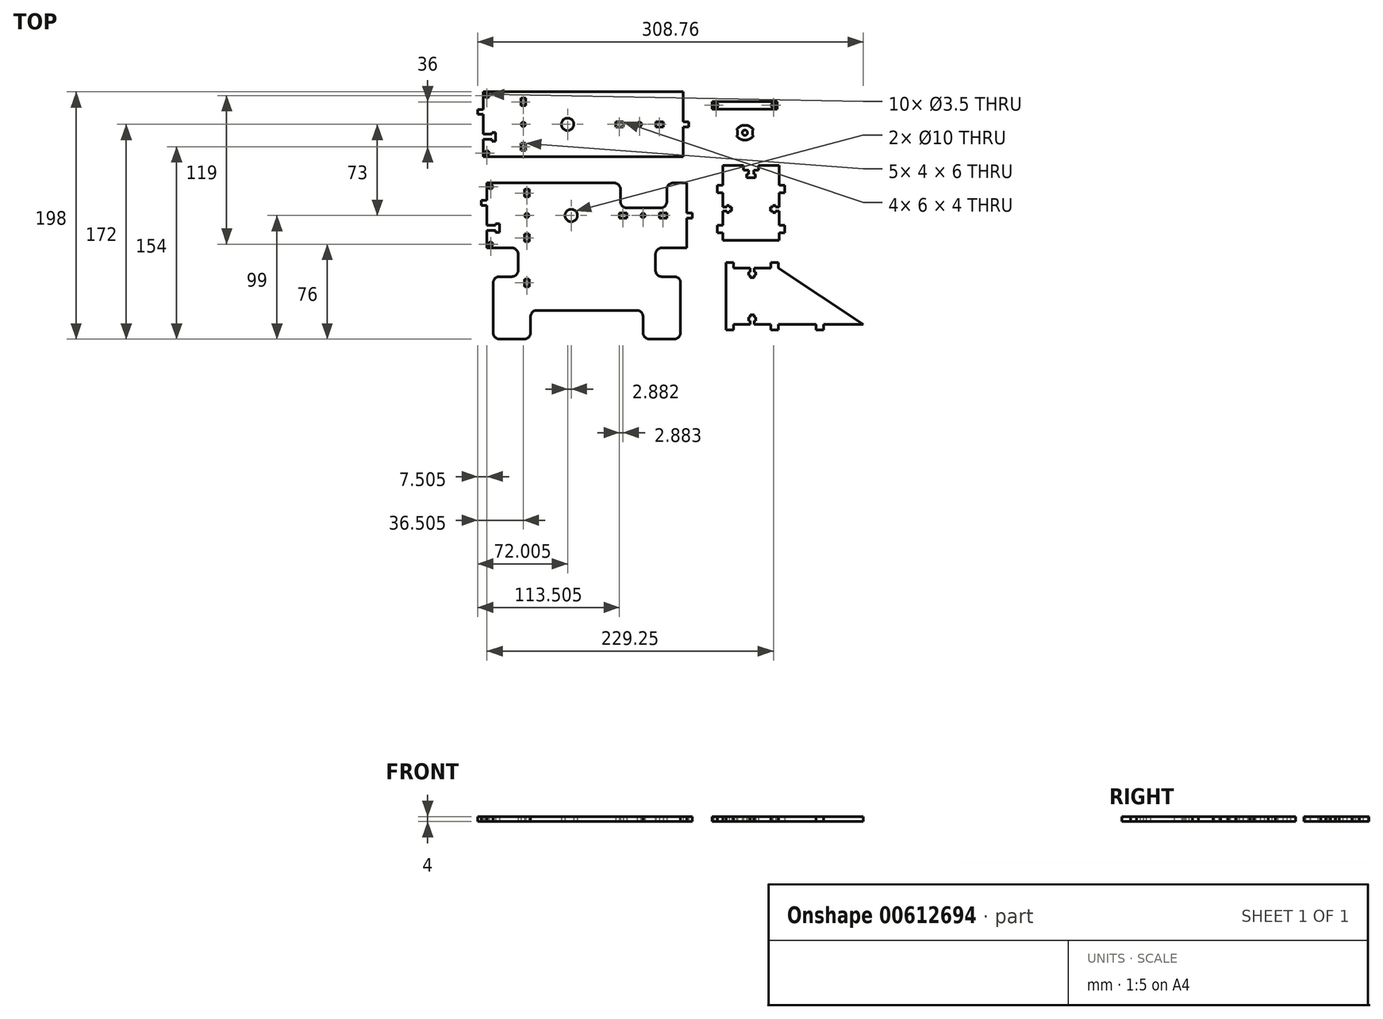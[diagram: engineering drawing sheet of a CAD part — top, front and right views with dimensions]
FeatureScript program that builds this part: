
annotation { "Feature Type Name" : "Feature", "Feature Type Description" : "" }
export const myFeature = defineFeature(function(context is Context, id is Id, definition is map)
    precondition{}
    {
        {
            var Q0;
            Q0=qCreatedBy(makeId("Top.planeOp"),FACE);
            var sketch = newSketch(context, id + "F0", { "sketchPlane" : qUnion([Q0])});
            skLineSegment(sketch, "E0", {"start": v(-149.88, 65.1) * mm, "end": v(-149.88, 81) * mm});
            skLineSegment(sketch, "E1", {"start": v(-149.88, 47) * mm, "end": v(-149.88, 60.9) * mm});
            skLineSegment(sketch, "E2", {"start": v(-149.88, 85) * mm, "end": v(-149.88, 99) * mm});
            skLineSegment(sketch, "E3", {"start": v(-147, -26) * mm, "end": v(-147, -12.1) * mm});
            skLineSegment(sketch, "E4", {"start": v(-147, -7.9) * mm, "end": v(-147, 8) * mm});
            skLineSegment(sketch, "E5", {"start": v(-147, 12) * mm, "end": v(-147, 26) * mm});
            skLineSegment(sketch, "E6", {"start": v(10.12, 75) * mm, "end": v(10.12, 99) * mm});
            skLineSegment(sketch, "E7", {"start": v(10.12, 47) * mm, "end": v(10.12, 71) * mm});
            skLineSegment(sketch, "E8", {"start": v(13, -26) * mm, "end": v(13, -2) * mm});
            skLineSegment(sketch, "E9", {"start": v(13, 2) * mm, "end": v(13, 26) * mm});
            skLineSegment(sketch, "E10", {"start": v(-147, 26) * mm, "end": v(-45, 26) * mm});
            skArc(sketch, "E11", {"start": v(-45, 26) * mm, "mid": v(-41.46, 24.54) * mm, "end": v(-40, 21) * mm});
            skLineSegment(sketch, "E12", {"start": v(-40, 21) * mm, "end": v(-40, 11) * mm});
            skArc(sketch, "E13", {"start": v(-40, 11) * mm, "mid": v(-38.53, 7.46) * mm, "end": v(-35, 6) * mm});
            skLineSegment(sketch, "E14", {"start": v(-35, 6) * mm, "end": v(-8, 6) * mm});
            skArc(sketch, "E15", {"start": v(-8, 6) * mm, "mid": v(-4.46, 7.46) * mm, "end": v(-3, 11) * mm});
            skLineSegment(sketch, "E16", {"start": v(-3, 11) * mm, "end": v(-3, 21) * mm});
            skArc(sketch, "E17", {"start": v(-3, 21) * mm, "mid": v(-1.53, 24.54) * mm, "end": v(2, 26) * mm});
            skLineSegment(sketch, "E18", {"start": v(2, 26) * mm, "end": v(13, 26) * mm});
            skLineSegment(sketch, "E19", {"start": v(-17, -99) * mm, "end": v(3, -99) * mm});
            skArc(sketch, "E20", {"start": v(3, -99) * mm, "mid": v(6.54, -97.54) * mm, "end": v(8, -94) * mm});
            skLineSegment(sketch, "E21", {"start": v(8, -94) * mm, "end": v(8, -54) * mm});
            skArc(sketch, "E22", {"start": v(8, -54) * mm, "mid": v(6.54, -50.46) * mm, "end": v(3, -49) * mm});
            skLineSegment(sketch, "E23", {"start": v(3, -49) * mm, "end": v(-7, -49) * mm});
            skArc(sketch, "E24", {"start": v(-7, -49) * mm, "mid": v(-10.53, -47.54) * mm, "end": v(-12, -44) * mm});
            skLineSegment(sketch, "E25", {"start": v(-12, -44) * mm, "end": v(-12, -31) * mm});
            skArc(sketch, "E26", {"start": v(-12, -31) * mm, "mid": v(-10.53, -27.46) * mm, "end": v(-7, -26) * mm});
            skLineSegment(sketch, "E27", {"start": v(-7, -26) * mm, "end": v(13, -26) * mm});
            skLineSegment(sketch, "E28", {"start": v(-147, -26) * mm, "end": v(-127, -26) * mm});
            skArc(sketch, "E29", {"start": v(-127, -26) * mm, "mid": v(-123.46, -27.46) * mm, "end": v(-122, -31) * mm});
            skLineSegment(sketch, "E30", {"start": v(-122, -31) * mm, "end": v(-122, -44) * mm});
            skArc(sketch, "E31", {"start": v(-122, -44) * mm, "mid": v(-123.46, -47.54) * mm, "end": v(-127, -49) * mm});
            skLineSegment(sketch, "E32", {"start": v(-127, -49) * mm, "end": v(-137, -49) * mm});
            skArc(sketch, "E33", {"start": v(-137, -49) * mm, "mid": v(-140.53, -50.46) * mm, "end": v(-142, -54) * mm});
            skLineSegment(sketch, "E34", {"start": v(-142, -54) * mm, "end": v(-142, -94) * mm});
            skArc(sketch, "E35", {"start": v(-142, -94) * mm, "mid": v(-140.53, -97.54) * mm, "end": v(-137, -99) * mm});
            skLineSegment(sketch, "E36", {"start": v(-137, -99) * mm, "end": v(-117, -99) * mm});
            skArc(sketch, "E37", {"start": v(-117, -99) * mm, "mid": v(-113.46, -97.54) * mm, "end": v(-112, -94) * mm});
            skLineSegment(sketch, "E38", {"start": v(-112, -94) * mm, "end": v(-112, -81) * mm});
            skArc(sketch, "E39", {"start": v(-112, -81) * mm, "mid": v(-110.53, -77.46) * mm, "end": v(-107, -76) * mm});
            skLineSegment(sketch, "E40", {"start": v(-107, -76) * mm, "end": v(-27, -76) * mm});
            skArc(sketch, "E41", {"start": v(-27, -76) * mm, "mid": v(-23.46, -77.46) * mm, "end": v(-22, -81) * mm});
            skLineSegment(sketch, "E42", {"start": v(-22, -81) * mm, "end": v(-22, -94) * mm});
            skArc(sketch, "E43", {"start": v(-22, -94) * mm, "mid": v(-20.53, -97.54) * mm, "end": v(-17, -99) * mm});
            skLineSegment(sketch, "E44", {"start": v(-5.88, 71) * mm, "end": v(-11.88, 71) * mm});
            skLineSegment(sketch, "E45", {"start": v(-37.88, 71) * mm, "end": v(-43.88, 71) * mm});
            skLineSegment(sketch, "E46", {"start": v(-119.88, 88) * mm, "end": v(-119.88, 94) * mm});
            skLineSegment(sketch, "E47", {"start": v(-119.88, 52) * mm, "end": v(-119.88, 58) * mm});
            skLineSegment(sketch, "E48", {"start": v(-35, -2) * mm, "end": v(-41, -2) * mm});
            skLineSegment(sketch, "E49", {"start": v(-3, -2) * mm, "end": v(-9, -2) * mm});
            skLineSegment(sketch, "E50", {"start": v(-117, -21) * mm, "end": v(-117, -15) * mm});
            skLineSegment(sketch, "E51", {"start": v(-117, 15) * mm, "end": v(-117, 21) * mm});
            skLineSegment(sketch, "E52", {"start": v(-117, -57) * mm, "end": v(-117, -51) * mm});
            skLineSegment(sketch, "E53", {"start": v(-5.88, 75) * mm, "end": v(-11.88, 75) * mm});
            skLineSegment(sketch, "E54", {"start": v(-37.88, 75) * mm, "end": v(-43.88, 75) * mm});
            skLineSegment(sketch, "E55", {"start": v(-115.88, 88) * mm, "end": v(-115.88, 94) * mm});
            skLineSegment(sketch, "E56", {"start": v(-115.88, 52) * mm, "end": v(-115.88, 58) * mm});
            skLineSegment(sketch, "E57", {"start": v(-35, 2) * mm, "end": v(-41, 2) * mm});
            skLineSegment(sketch, "E58", {"start": v(-3, 2) * mm, "end": v(-9, 2) * mm});
            skLineSegment(sketch, "E59", {"start": v(-113, -21) * mm, "end": v(-113, -15) * mm});
            skLineSegment(sketch, "E60", {"start": v(-113, 15) * mm, "end": v(-113, 21) * mm});
            skLineSegment(sketch, "E61", {"start": v(-113, -57) * mm, "end": v(-113, -51) * mm});
            skLineSegment(sketch, "E62", {"start": v(-5.88, 71) * mm, "end": v(-5.88, 75) * mm});
            skLineSegment(sketch, "E63", {"start": v(-43.88, 71) * mm, "end": v(-43.88, 75) * mm});
            skLineSegment(sketch, "E64", {"start": v(-119.88, 94) * mm, "end": v(-115.88, 94) * mm});
            skLineSegment(sketch, "E65", {"start": v(-119.88, 52) * mm, "end": v(-115.88, 52) * mm});
            skLineSegment(sketch, "E66", {"start": v(-117, -57) * mm, "end": v(-113, -57) * mm});
            skLineSegment(sketch, "E67", {"start": v(-117, -21) * mm, "end": v(-113, -21) * mm});
            skLineSegment(sketch, "E68", {"start": v(-117, 21) * mm, "end": v(-113, 21) * mm});
            skLineSegment(sketch, "E69", {"start": v(-41, -2) * mm, "end": v(-41, 2) * mm});
            skLineSegment(sketch, "E70", {"start": v(-3, -2) * mm, "end": v(-3, 2) * mm});
            skLineSegment(sketch, "E71", {"start": v(37.5, 24.13) * mm, "end": v(42, 24.13) * mm});
            skLineSegment(sketch, "E72", {"start": v(87, 24.13) * mm, "end": v(91.5, 24.13) * mm});
            skLineSegment(sketch, "E73", {"start": v(86.38, -91.75) * mm, "end": v(86.38, -87.25) * mm});
            skLineSegment(sketch, "E74", {"start": v(86.38, -42.25) * mm, "end": v(86.38, -37.75) * mm});
            skLineSegment(sketch, "E75", {"start": v(122.38, -91.75) * mm, "end": v(122.38, -87.25) * mm});
            skLineSegment(sketch, "E76", {"start": v(-11.88, 71) * mm, "end": v(-11.88, 75) * mm});
            skLineSegment(sketch, "E77", {"start": v(-37.88, 71) * mm, "end": v(-37.88, 75) * mm});
            skLineSegment(sketch, "E78", {"start": v(-119.88, 88) * mm, "end": v(-115.88, 88) * mm});
            skLineSegment(sketch, "E79", {"start": v(-119.88, 58) * mm, "end": v(-115.88, 58) * mm});
            skLineSegment(sketch, "E80", {"start": v(-117, -51) * mm, "end": v(-113, -51) * mm});
            skLineSegment(sketch, "E81", {"start": v(-117, -15) * mm, "end": v(-113, -15) * mm});
            skLineSegment(sketch, "E82", {"start": v(-117, 15) * mm, "end": v(-113, 15) * mm});
            skLineSegment(sketch, "E83", {"start": v(-35, -2) * mm, "end": v(-35, 2) * mm});
            skLineSegment(sketch, "E84", {"start": v(-9, -2) * mm, "end": v(-9, 2) * mm});
            skLineSegment(sketch, "E85", {"start": v(37.5, 18.13) * mm, "end": v(42, 18.13) * mm});
            skLineSegment(sketch, "E86", {"start": v(87, 18.13) * mm, "end": v(91.5, 18.13) * mm});
            skLineSegment(sketch, "E87", {"start": v(50.38, -91.75) * mm, "end": v(50.38, -87.25) * mm});
            skLineSegment(sketch, "E88", {"start": v(50.38, -42.25) * mm, "end": v(50.38, -37.75) * mm});
            skLineSegment(sketch, "E89", {"start": v(80.38, -91.75) * mm, "end": v(80.38, -87.25) * mm});
            skLineSegment(sketch, "E90", {"start": v(80.38, -42.25) * mm, "end": v(80.38, -37.75) * mm});
            skLineSegment(sketch, "E91", {"start": v(116.38, -91.75) * mm, "end": v(116.38, -87.25) * mm});
            skCircle(sketch, "E92", {"center": v(-24.88, 73) * mm, "radius": 1.75 * mm});
            skCircle(sketch, "E93", {"center": v(-117.88, 73) * mm, "radius": 1.75 * mm});
            skCircle(sketch, "E94", {"center": v(-22, 0) * mm, "radius": 1.75 * mm});
            skCircle(sketch, "E95", {"center": v(-115, 0) * mm, "radius": 1.75 * mm});
            skCircle(sketch, "E96", {"center": v(-82.38, 73) * mm, "radius": 5 * mm});
            skCircle(sketch, "E97", {"center": v(-79.5, 0) * mm, "radius": 5 * mm});
            skLineSegment(sketch, "E98", {"start": v(10.12, 75) * mm, "end": v(14.62, 75) * mm});
            skLineSegment(sketch, "E99", {"start": v(13, 2) * mm, "end": v(17.5, 2) * mm});
            skLineSegment(sketch, "E100", {"start": v(10.12, 71) * mm, "end": v(14.62, 71) * mm});
            skLineSegment(sketch, "E101", {"start": v(13, -2) * mm, "end": v(17.5, -2) * mm});
            skLineSegment(sketch, "E102", {"start": v(14.62, 75) * mm, "end": v(14.62, 71) * mm});
            skLineSegment(sketch, "E103", {"start": v(17.5, 2) * mm, "end": v(17.5, -2) * mm});
            skLineSegment(sketch, "E104", {"start": v(-154.38, 85) * mm, "end": v(-149.88, 85) * mm});
            skLineSegment(sketch, "E105", {"start": v(-151.5, 12) * mm, "end": v(-147, 12) * mm});
            skLineSegment(sketch, "E106", {"start": v(-154.38, 81) * mm, "end": v(-149.88, 81) * mm});
            skLineSegment(sketch, "E107", {"start": v(-151.5, 8) * mm, "end": v(-147, 8) * mm});
            skLineSegment(sketch, "E108", {"start": v(-154.38, 85) * mm, "end": v(-154.38, 81) * mm});
            skLineSegment(sketch, "E109", {"start": v(-151.5, 12) * mm, "end": v(-151.5, 8) * mm});
            skLineSegment(sketch, "E110", {"start": v(68.05, 30.13) * mm, "end": v(60.95, 30.13) * mm});
            skLineSegment(sketch, "E111", {"start": v(-139.88, 59.45) * mm, "end": v(-139.88, 66.55) * mm});
            skLineSegment(sketch, "E112", {"start": v(-137, -13.55) * mm, "end": v(-137, -6.45) * mm});
            skCircle(sketch, "E113", {"center": v(-146.88, 96) * mm, "radius": 1.75 * mm});
            skCircle(sketch, "E114", {"center": v(-144, 23) * mm, "radius": 1.75 * mm});
            skCircle(sketch, "E115", {"center": v(-146.88, 50) * mm, "radius": 1.75 * mm});
            skCircle(sketch, "E116", {"center": v(-144, -23) * mm, "radius": 1.75 * mm});
            skLineSegment(sketch, "E117", {"start": v(42, 3.53) * mm, "end": v(42, -7.87) * mm});
            skLineSegment(sketch, "E118", {"start": v(42, 18.13) * mm, "end": v(42, 6.73) * mm});
            skLineSegment(sketch, "E119", {"start": v(154.38, -87.25) * mm, "end": v(122.38, -87.25) * mm});
            skLineSegment(sketch, "E120", {"start": v(63.78, -87.25) * mm, "end": v(50.38, -87.25) * mm});
            skLineSegment(sketch, "E121", {"start": v(80.38, -87.25) * mm, "end": v(66.97, -87.25) * mm});
            skLineSegment(sketch, "E122", {"start": v(116.38, -87.25) * mm, "end": v(86.38, -87.25) * mm});
            skLineSegment(sketch, "E123", {"start": v(87, -7.87) * mm, "end": v(87, 3.53) * mm});
            skLineSegment(sketch, "E124", {"start": v(87, 6.73) * mm, "end": v(87, 18.13) * mm});
            skLineSegment(sketch, "E125", {"start": v(50.38, -42.25) * mm, "end": v(63.78, -42.25) * mm});
            skLineSegment(sketch, "E126", {"start": v(66.97, -42.25) * mm, "end": v(80.38, -42.25) * mm});
            skLineSegment(sketch, "E127", {"start": v(91.5, 18.13) * mm, "end": v(91.5, 24.13) * mm});
            skLineSegment(sketch, "E128", {"start": v(37.5, 24.13) * mm, "end": v(37.5, 18.13) * mm});
            skLineSegment(sketch, "E129", {"start": v(45, 7.88) * mm, "end": v(45, 6.73) * mm});
            skLineSegment(sketch, "E130", {"start": v(45, 3.53) * mm, "end": v(45, 2.38) * mm});
            skLineSegment(sketch, "E131", {"start": v(68.12, -45.25) * mm, "end": v(66.97, -45.25) * mm});
            skLineSegment(sketch, "E132", {"start": v(63.78, -45.25) * mm, "end": v(62.62, -45.25) * mm});
            skLineSegment(sketch, "E133", {"start": v(68.12, -84.25) * mm, "end": v(66.97, -84.25) * mm});
            skLineSegment(sketch, "E134", {"start": v(63.78, -84.25) * mm, "end": v(62.62, -84.25) * mm});
            skLineSegment(sketch, "E135", {"start": v(47, 7.88) * mm, "end": v(47, 6.73) * mm});
            skLineSegment(sketch, "E136", {"start": v(47, 3.53) * mm, "end": v(47, 2.38) * mm});
            skLineSegment(sketch, "E137", {"start": v(68.12, -47.85) * mm, "end": v(66.97, -47.85) * mm});
            skLineSegment(sketch, "E138", {"start": v(63.78, -47.85) * mm, "end": v(62.62, -47.85) * mm});
            skLineSegment(sketch, "E139", {"start": v(68.12, -81.65) * mm, "end": v(66.97, -81.65) * mm});
            skLineSegment(sketch, "E140", {"start": v(63.78, -81.65) * mm, "end": v(62.62, -81.65) * mm});
            skLineSegment(sketch, "E141", {"start": v(49, 6.73) * mm, "end": v(49, 3.53) * mm});
            skLineSegment(sketch, "E142", {"start": v(66.97, -49.85) * mm, "end": v(63.78, -49.85) * mm});
            skLineSegment(sketch, "E143", {"start": v(66.97, -79.65) * mm, "end": v(63.78, -79.65) * mm});
            skLineSegment(sketch, "E144", {"start": v(45, 2.38) * mm, "end": v(47, 2.38) * mm});
            skLineSegment(sketch, "E145", {"start": v(62.62, -45.25) * mm, "end": v(62.62, -47.85) * mm});
            skLineSegment(sketch, "E146", {"start": v(62.62, -84.25) * mm, "end": v(62.62, -81.65) * mm});
            skLineSegment(sketch, "E147", {"start": v(45, 7.88) * mm, "end": v(47, 7.88) * mm});
            skLineSegment(sketch, "E148", {"start": v(68.12, -84.25) * mm, "end": v(68.12, -81.65) * mm});
            skLineSegment(sketch, "E149", {"start": v(68.12, -45.25) * mm, "end": v(68.12, -47.85) * mm});
            skLineSegment(sketch, "E150", {"start": v(86.38, -42.25) * mm, "end": v(154.37, -87.25) * mm});
            skLineSegment(sketch, "E151", {"start": v(70.5, 40.13) * mm, "end": v(87, 40.13) * mm});
            skLineSegment(sketch, "E152", {"start": v(42, 40.13) * mm, "end": v(58.5, 40.13) * mm});
            skLineSegment(sketch, "E153", {"start": v(87, 24.13) * mm, "end": v(87, 40.13) * mm});
            skLineSegment(sketch, "E154", {"start": v(42, 24.13) * mm, "end": v(42, 40.13) * mm});
            skLineSegment(sketch, "E155", {"start": v(37.5, -7.87) * mm, "end": v(42, -7.87) * mm});
            skLineSegment(sketch, "E156", {"start": v(87, -7.87) * mm, "end": v(91.5, -7.87) * mm});
            skLineSegment(sketch, "E157", {"start": v(37.5, -13.87) * mm, "end": v(42, -13.87) * mm});
            skLineSegment(sketch, "E158", {"start": v(87, -13.87) * mm, "end": v(91.5, -13.87) * mm});
            skLineSegment(sketch, "E159", {"start": v(91.5, -13.87) * mm, "end": v(91.5, -7.87) * mm});
            skLineSegment(sketch, "E160", {"start": v(42, -19.87) * mm, "end": v(87, -19.87) * mm});
            skLineSegment(sketch, "E161", {"start": v(85.38, 91.25) * mm, "end": v(85.38, 85.25) * mm});
            skLineSegment(sketch, "E162", {"start": v(33.38, 91.25) * mm, "end": v(33.38, 85.25) * mm});
            skCircle(sketch, "E163", {"center": v(36.38, 88.25) * mm, "radius": 1.75 * mm});
            skCircle(sketch, "E164", {"center": v(82.38, 88.25) * mm, "radius": 1.75 * mm});
            skLineSegment(sketch, "E165", {"start": v(44.38, -37.75) * mm, "end": v(50.38, -37.75) * mm});
            skLineSegment(sketch, "E166", {"start": v(37.5, -13.87) * mm, "end": v(37.5, -7.87) * mm});
            skLineSegment(sketch, "E167", {"start": v(60.95, 33.13) * mm, "end": v(60.95, 30.13) * mm});
            skLineSegment(sketch, "E168", {"start": v(-142.88, 66.55) * mm, "end": v(-139.88, 66.55) * mm});
            skLineSegment(sketch, "E169", {"start": v(-140, -6.45) * mm, "end": v(-137, -6.45) * mm});
            skLineSegment(sketch, "E170", {"start": v(68.05, 33.13) * mm, "end": v(68.05, 30.13) * mm});
            skLineSegment(sketch, "E171", {"start": v(-142.88, 59.45) * mm, "end": v(-139.88, 59.45) * mm});
            skLineSegment(sketch, "E172", {"start": v(-140, -13.55) * mm, "end": v(-137, -13.55) * mm});
            skLineSegment(sketch, "E173", {"start": v(68.05, 33.13) * mm, "end": v(66.6, 33.13) * mm});
            skLineSegment(sketch, "E174", {"start": v(62.4, 33.13) * mm, "end": v(60.95, 33.13) * mm});
            skLineSegment(sketch, "E175", {"start": v(-142.88, 59.45) * mm, "end": v(-142.88, 60.9) * mm});
            skLineSegment(sketch, "E176", {"start": v(-142.88, 65.1) * mm, "end": v(-142.88, 66.55) * mm});
            skLineSegment(sketch, "E177", {"start": v(-140, -7.9) * mm, "end": v(-140, -6.45) * mm});
            skLineSegment(sketch, "E178", {"start": v(-140, -13.55) * mm, "end": v(-140, -12.1) * mm});
            skLineSegment(sketch, "E179", {"start": v(62.4, 36.13) * mm, "end": v(62.4, 33.13) * mm});
            skLineSegment(sketch, "E180", {"start": v(-149.88, 65.1) * mm, "end": v(-142.88, 65.1) * mm});
            skLineSegment(sketch, "E181", {"start": v(-147, -7.9) * mm, "end": v(-140, -7.9) * mm});
            skLineSegment(sketch, "E182", {"start": v(66.6, 36.13) * mm, "end": v(66.6, 33.13) * mm});
            skLineSegment(sketch, "E183", {"start": v(-149.88, 60.9) * mm, "end": v(-142.88, 60.9) * mm});
            skLineSegment(sketch, "E184", {"start": v(-147, -12.1) * mm, "end": v(-140, -12.1) * mm});
            skLineSegment(sketch, "E185", {"start": v(42, 6.73) * mm, "end": v(45, 6.73) * mm});
            skLineSegment(sketch, "E186", {"start": v(47, 6.73) * mm, "end": v(49, 6.73) * mm});
            skLineSegment(sketch, "E187", {"start": v(47, 3.53) * mm, "end": v(49, 3.53) * mm});
            skLineSegment(sketch, "E188", {"start": v(42, 3.53) * mm, "end": v(45, 3.53) * mm});
            skLineSegment(sketch, "E189", {"start": v(66.97, -42.25) * mm, "end": v(66.97, -45.25) * mm});
            skLineSegment(sketch, "E190", {"start": v(63.78, -42.25) * mm, "end": v(63.78, -45.25) * mm});
            skLineSegment(sketch, "E191", {"start": v(63.78, -47.85) * mm, "end": v(63.78, -49.85) * mm});
            skLineSegment(sketch, "E192", {"start": v(66.97, -47.85) * mm, "end": v(66.97, -49.85) * mm});
            skLineSegment(sketch, "E193", {"start": v(66.97, -81.65) * mm, "end": v(66.97, -79.65) * mm});
            skLineSegment(sketch, "E194", {"start": v(63.78, -81.65) * mm, "end": v(63.78, -79.65) * mm});
            skLineSegment(sketch, "E195", {"start": v(63.78, -87.25) * mm, "end": v(63.78, -84.25) * mm});
            skLineSegment(sketch, "E196", {"start": v(66.97, -87.25) * mm, "end": v(66.97, -84.25) * mm});
            skLineSegment(sketch, "E197", {"start": v(44.38, -91.75) * mm, "end": v(44.38, -37.75) * mm});
            skLineSegment(sketch, "E198", {"start": v(80.38, -37.75) * mm, "end": v(86.38, -37.75) * mm});
            skLineSegment(sketch, "E199", {"start": v(-149.88, 99) * mm, "end": v(10.12, 99) * mm});
            skLineSegment(sketch, "E200", {"start": v(44.38, -91.75) * mm, "end": v(50.38, -91.75) * mm});
            skLineSegment(sketch, "E201", {"start": v(116.38, -91.75) * mm, "end": v(122.38, -91.75) * mm});
            skLineSegment(sketch, "E202", {"start": v(80.38, -91.75) * mm, "end": v(86.38, -91.75) * mm});
            skLineSegment(sketch, "E203", {"start": v(42, -13.87) * mm, "end": v(42, -19.87) * mm});
            skLineSegment(sketch, "E204", {"start": v(87, -13.87) * mm, "end": v(87, -19.87) * mm});
            skLineSegment(sketch, "E205", {"start": v(-149.88, 47) * mm, "end": v(10.12, 47) * mm});
            skLineSegment(sketch, "E206", {"start": v(33.38, 91.25) * mm, "end": v(85.38, 91.25) * mm});
            skLineSegment(sketch, "E207", {"start": v(33.38, 85.25) * mm, "end": v(85.38, 85.25) * mm});
            skLineSegment(sketch, "E208", {"start": v(58.5, 40.13) * mm, "end": v(58.5, 36.13) * mm});
            skLineSegment(sketch, "E209", {"start": v(58.5, 36.13) * mm, "end": v(62.4, 36.13) * mm});
            skLineSegment(sketch, "E210", {"start": v(70.5, 36.13) * mm, "end": v(70.5, 40.13) * mm});
            skLineSegment(sketch, "E211.trimOffspring", {"start": v(66.6, 36.13) * mm, "end": v(70.5, 36.13) * mm});
            skCircle(sketch, "E212", {"center": v(59.56, 66.28) * mm, "radius": 2.1 * mm});
            skLineSegment(sketch, "E213", {"start": v(48.94, 66.28) * mm, "end": v(70.17, 66.28) * mm, "construction": true});
            skLineSegment(sketch, "E214.left", {"start": v(65.56, 68.28) * mm, "end": v(65.56, 64.28) * mm});
            skLineSegment(sketch, "E214.right", {"start": v(53.56, 68.28) * mm, "end": v(53.56, 64.28) * mm});
            skArc(sketch, "E215", {"start": v(66.56, 68.28) * mm, "mid": v(59.56, 72.28) * mm, "end": v(52.56, 68.28) * mm});
            skArc(sketch, "E216", {"start": v(52.56, 64.28) * mm, "mid": v(59.56, 60.28) * mm, "end": v(66.56, 64.28) * mm});
            skLineSegment(sketch, "E217", {"start": v(59.56, 68.4) * mm, "end": v(59.56, 66.28) * mm, "construction": true});
            skLineSegment(sketch, "E218", {"start": v(59.56, 64.16) * mm, "end": v(59.56, 66.28) * mm, "construction": true});
            skLineSegment(sketch, "E219", {"start": v(52.56, 68.28) * mm, "end": v(53.56, 68.28) * mm});
            skLineSegment(sketch, "E220", {"start": v(52.56, 64.28) * mm, "end": v(53.56, 64.28) * mm});
            skLineSegment(sketch, "E221", {"start": v(65.56, 64.28) * mm, "end": v(66.56, 64.28) * mm});
            skLineSegment(sketch, "E222", {"start": v(65.56, 68.28) * mm, "end": v(66.56, 68.28) * mm});
            skCircle(sketch, "E223", {"center": v(59.56, 66.28) * mm, "radius": 6 * mm, "construction": true});
            skLineSegment(sketch, "E224", {"start": v(64.5, 30.13) * mm, "end": v(64.5, -19.87) * mm, "construction": true});
            skLineSegment(sketch, "E225.MirrorCS", {"start": v(84, 7.88) * mm, "end": v(84, 6.73) * mm});
            skLineSegment(sketch, "E226.MirrorCS", {"start": v(82, 7.88) * mm, "end": v(82, 6.73) * mm});
            skLineSegment(sketch, "E227.MirrorCS", {"start": v(84, 7.88) * mm, "end": v(82, 7.88) * mm});
            skLineSegment(sketch, "E228.MirrorCS", {"start": v(84, 2.38) * mm, "end": v(82, 2.38) * mm});
            skLineSegment(sketch, "E229.MirrorCS", {"start": v(84, 3.53) * mm, "end": v(84, 2.38) * mm});
            skLineSegment(sketch, "E230.MirrorCS", {"start": v(82, 3.53) * mm, "end": v(80, 3.53) * mm});
            skLineSegment(sketch, "E231.MirrorCS", {"start": v(82, 3.53) * mm, "end": v(82, 2.38) * mm});
            skLineSegment(sketch, "E232.MirrorCS", {"start": v(82, 6.73) * mm, "end": v(80, 6.73) * mm});
            skLineSegment(sketch, "E233.MirrorCS", {"start": v(87, 3.53) * mm, "end": v(84, 3.53) * mm});
            skLineSegment(sketch, "E234.MirrorCS", {"start": v(80, 6.73) * mm, "end": v(80, 3.53) * mm});
            skLineSegment(sketch, "E235.MirrorCS", {"start": v(87, 6.73) * mm, "end": v(84, 6.73) * mm});
            skSolve(sketch);
        }
        {
            var Q0;
            Q0=makeQuery(id+"F0.imprint","IMPRINT",FACE,{"disambiguationData":[TD([[makeQuery(id+"F0.imprint","IMPRINT",EDGE,{"derivedFrom":sQuery(id+"F0.wireOp",EDGE,"E0")}),-1.0]])]});
            var Q1;
            Q1=makeQuery(id+"F0.imprint","IMPRINT",FACE,{"disambiguationData":[TD([[makeQuery(id+"F0.imprint","IMPRINT",EDGE,{"derivedFrom":sQuery(id+"F0.wireOp",EDGE,"E3")}),-1.0]])]});
            var Q2;
            Q2=makeQuery(id+"F0.imprint","IMPRINT",FACE,{"disambiguationData":[TD([[makeQuery(id+"F0.imprint","IMPRINT",EDGE,{"derivedFrom":sQuery(id+"F0.wireOp",EDGE,"E161")}),-1.0]])]});
            var Q3;
            Q3=makeQuery(id+"F0.imprint","IMPRINT",FACE,{"disambiguationData":[TD([[makeQuery(id+"F0.imprint","IMPRINT",EDGE,{"derivedFrom":sQuery(id+"F0.wireOp",EDGE,"E71")}),-1.0]])]});
            var Q4;
            Q4=makeQuery(id+"F0.imprint","IMPRINT",FACE,{"disambiguationData":[TD([[makeQuery(id+"F0.imprint","IMPRINT",EDGE,{"derivedFrom":sQuery(id+"F0.wireOp",EDGE,"E73")}),1.0]])]});
            var Q5;
            Q5=makeQuery(id+"F0.imprint","IMPRINT",FACE,{"disambiguationData":[TD([[makeQuery(id+"F0.imprint","IMPRINT",EDGE,{"derivedFrom":sQuery(id+"F0.wireOp",EDGE,"E212")}),-1.0]])]});
            extrude(context, id + "F1", {"entities" : qUnion([Q0, Q1, Q2, Q3, Q4, Q5]), "depth" : 4 * mm, "offsetDistance" : 25 * mm});
        }
    });
